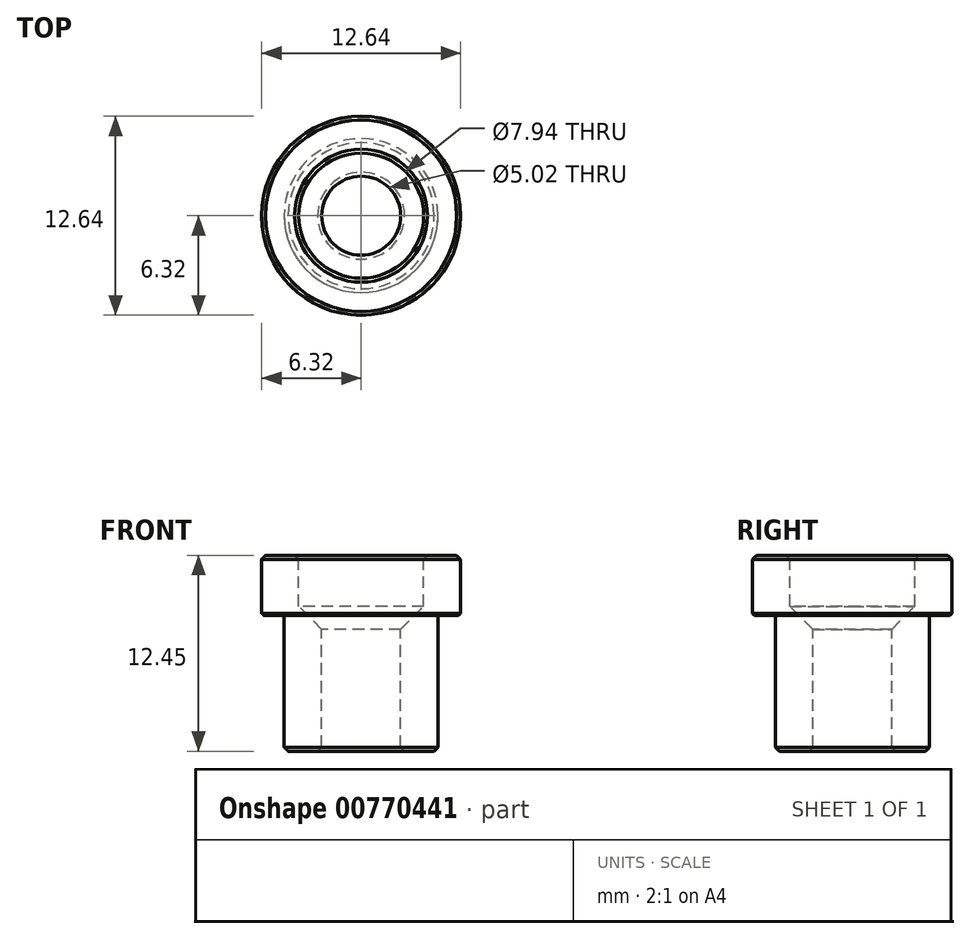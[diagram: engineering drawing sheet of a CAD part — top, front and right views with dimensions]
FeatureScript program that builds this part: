
annotation { "Feature Type Name" : "Feature", "Feature Type Description" : "" }
export const myFeature = defineFeature(function(context is Context, id is Id, definition is map)
    precondition{}
    {
        {
            var Q0;
            Q0=qCreatedBy(makeId("Front.planeOp"),FACE);
            var sketch = newSketch(context, id + "F0", { "sketchPlane" : qUnion([Q0])});
            skLineSegment(sketch, "E0", {"start": v(6.32, 0) * mm, "end": v(6.32, -3.81) * mm});
            skLineSegment(sketch, "E1", {"start": v(6.32, -3.81) * mm, "end": v(4.89, -3.81) * mm});
            skLineSegment(sketch, "E2", {"start": v(4.89, -3.81) * mm, "end": v(4.89, -12.45) * mm});
            skLineSegment(sketch, "E3", {"start": v(4.89, -12.45) * mm, "end": v(2.5, -12.45) * mm});
            skLineSegment(sketch, "E4", {"start": v(2.5, -12.45) * mm, "end": v(2.5, -2.16) * mm});
            skLineSegment(sketch, "E5", {"start": v(2.5, -2.16) * mm, "end": v(3.97, -2.16) * mm});
            skLineSegment(sketch, "E6", {"start": v(3.97, -2.16) * mm, "end": v(3.97, 0) * mm});
            skLineSegment(sketch, "E7", {"start": v(6.32, 0) * mm, "end": v(3.97, 0) * mm});
            skLineSegment(sketch, "E8", {"start": v(0, 0) * mm, "end": v(0, -21.43) * mm, "construction": true});
            skSolve(sketch);
        }
        {
            var Q0;
            Q0=makeQuery(id+"F0.imprint","IMPRINT",FACE,{"disambiguationData":[TD([[makeQuery(id+"F0.imprint","IMPRINT",EDGE,{"derivedFrom":sQuery(id+"F0.wireOp",EDGE,"E0")}),-1.0]])]});
            var Q1;
            Q1=sQuery(id+"F0.wireOp",EDGE,"E8");
            revolve(context, id + "F1", {"surfaceOperationType" : NewSurfaceOperationType.NEW, "entities" : qUnion([Q0]), "axis" : qUnion([Q1]), "revolveType" : RevolveType.FULL});
        }
        {
            var Q0;
            Q0=makeQuery(id+"F1.opRevolve","SWEPT_EDGE",EDGE,{"disambiguationData":[OSD([sQuery(id+"F0.wireOp",EDGE,"E0"),sQuery(id+"F0.wireOp",EDGE,"E7")])]});
            var Q1;
            Q1=makeQuery(id+"F1.opRevolve","SWEPT_EDGE",EDGE,{"disambiguationData":[OSD([sQuery(id+"F0.wireOp",EDGE,"E2"),sQuery(id+"F0.wireOp",EDGE,"E3")])]});
            var Q2;
            Q2=makeQuery(id+"F1.opRevolve","SWEPT_EDGE",EDGE,{"disambiguationData":[OSD([sQuery(id+"F0.wireOp",EDGE,"E3"),sQuery(id+"F0.wireOp",EDGE,"E4")])]});
            var Q3;
            Q3=makeQuery(id+"F1.opRevolve","SWEPT_EDGE",EDGE,{"disambiguationData":[OSD([sQuery(id+"F0.wireOp",EDGE,"E6"),sQuery(id+"F0.wireOp",EDGE,"E7")])]});
            chamfer(context, id + "F2", {"entities" : qUnion([Q0, Q1, Q2, Q3]), "width" : 0.25 * mm, "tangentPropagation" : true});
        }
        {
            var Q0;
            Q0=makeQuery(id+"F1.opRevolve","SWEPT_EDGE",EDGE,{"disambiguationData":[OSD([sQuery(id+"F0.wireOp",EDGE,"E4"),sQuery(id+"F0.wireOp",EDGE,"E5")])]});
            chamfer(context, id + "F3", {"entities" : qUnion([Q0]), "width" : 2.54 * mm, "tangentPropagation" : true});
        }
        {
            var Q0;
            Q0=makeQuery(id+"F1.opRevolve","SWEPT_EDGE",EDGE,{"disambiguationData":[OSD([sQuery(id+"F0.wireOp",EDGE,"E0"),sQuery(id+"F0.wireOp",EDGE,"E1")])]});
            chamfer(context, id + "F4", {"entities" : qUnion([Q0]), "width" : 0.13 * mm, "tangentPropagation" : true});
        }
    });
